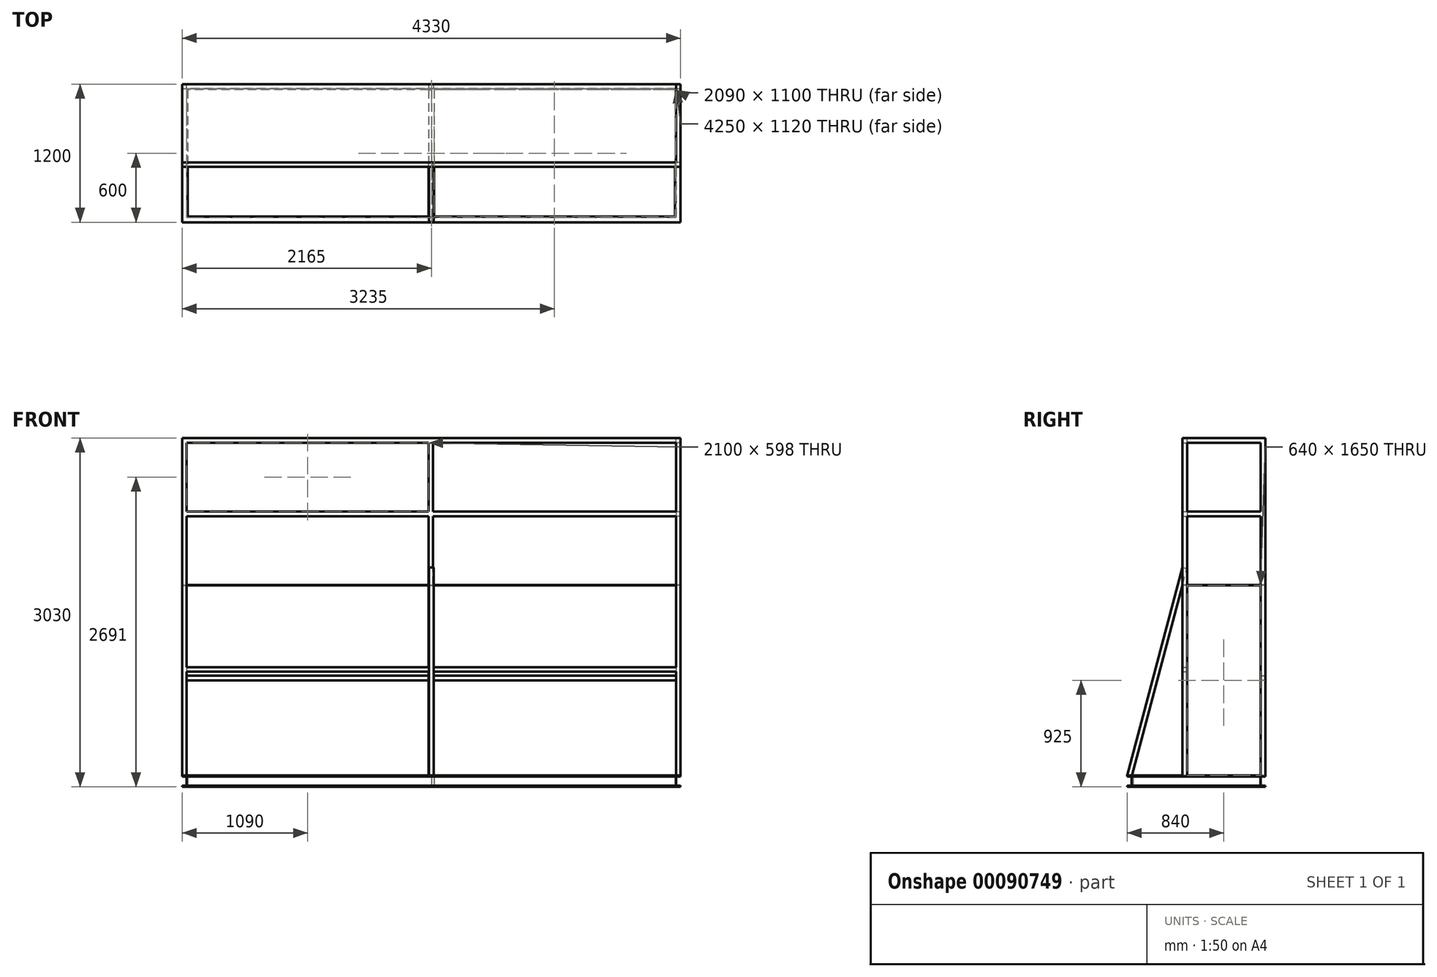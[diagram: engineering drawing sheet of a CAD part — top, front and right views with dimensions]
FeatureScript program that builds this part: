
annotation { "Feature Type Name" : "Feature", "Feature Type Description" : "" }
export const myFeature = defineFeature(function(context is Context, id is Id, definition is map)
    precondition{}
    {
        {
            var Q0;
            Q0=qCreatedBy(makeId("Top.planeOp"),FACE);
            var sketch = newSketch(context, id + "F0", { "sketchPlane" : qUnion([Q0])});
            skLineSegment(sketch, "E0.rect.bottom", {"start": v(2165, 600) * mm, "end": v(-2165, 600) * mm});
            skLineSegment(sketch, "E0.rect.top", {"start": v(2165, -600) * mm, "end": v(-2165, -600) * mm});
            skLineSegment(sketch, "E0.rect.left", {"start": v(2165, 600) * mm, "end": v(2165, -600) * mm});
            skLineSegment(sketch, "E0.rect.right", {"start": v(-2165, 600) * mm, "end": v(-2165, -600) * mm});
            skPoint(sketch, "E0.rect.middle", {"position": v(0, 0) * mm});
            skLineSegment(sketch, "E1.rect.bottom", {"start": v(2115, 550) * mm, "end": v(25, 550) * mm});
            skLineSegment(sketch, "E1.rect.top", {"start": v(2115, -550) * mm, "end": v(25, -550) * mm});
            skLineSegment(sketch, "E1.rect.left", {"start": v(2115, 550) * mm, "end": v(2115, -550) * mm});
            skLineSegment(sketch, "E1.rect.right", {"start": v(-2115, 550) * mm, "end": v(-2115, -550) * mm});
            skLineSegment(sketch, "E2.rect.left", {"start": v(25, 550) * mm, "end": v(25, -550) * mm});
            skLineSegment(sketch, "E2.rect.right", {"start": v(-25, 550) * mm, "end": v(-25, -550) * mm});
            skLineSegment(sketch, "E3.trimOffspring", {"start": v(-25, 550) * mm, "end": v(-2115, 550) * mm});
            skLineSegment(sketch, "E4.trimOffspring", {"start": v(-25, -550) * mm, "end": v(-2115, -550) * mm});
            skSolve(sketch);
        }
        {
            var Q0;
            Q0=makeQuery(id+"F0.imprint","IMPRINT",FACE,{"disambiguationData":[TD([[makeQuery(id+"F0.imprint","IMPRINT",EDGE,{"derivedFrom":sQuery(id+"F0.wireOp",EDGE,"E0.rect.bottom")}),1.0]])]});
            extrude(context, id + "F1", {"entities" : qUnion([Q0]), "depth" : 100 * mm});
        }
        {
            var Q0;
            Q0=makeQuery(id+"F1.opExtrude","SWEPT_FACE",FACE,{"disambiguationData":[OSD([sQuery(id+"F0.wireOp",EDGE,"E0.rect.right")])]});
            var sketch = newSketch(context, id + "F2", { "sketchPlane" : qUnion([Q0])});
            skLineSegment(sketch, "E5.bottom", {"start": v(-600, 90) * mm, "end": v(-560, 90) * mm});
            skLineSegment(sketch, "E5.top", {"start": v(-600, 10) * mm, "end": v(-560, 10) * mm});
            skLineSegment(sketch, "E5.left", {"start": v(-600, 90) * mm, "end": v(-600, 10) * mm});
            skLineSegment(sketch, "E5.right", {"start": v(-560, 90) * mm, "end": v(-560, 10) * mm});
            skLineSegment(sketch, "E6.bottom", {"start": v(600, 90) * mm, "end": v(560, 90) * mm});
            skLineSegment(sketch, "E6.top", {"start": v(600, 10) * mm, "end": v(560, 10) * mm});
            skLineSegment(sketch, "E6.left", {"start": v(600, 90) * mm, "end": v(600, 10) * mm});
            skLineSegment(sketch, "E6.right", {"start": v(560, 90) * mm, "end": v(560, 10) * mm});
            skSolve(sketch);
        }
        {
            var Q0;
            Q0=makeQuery(id+"F2.imprint","IMPRINT",FACE,{"disambiguationData":[TD([[makeQuery(id+"F2.imprint","IMPRINT",EDGE,{"derivedFrom":sQuery(id+"F2.wireOp",EDGE,"E5.bottom")}),-1.0]])]});
            var Q1;
            Q1=makeQuery(id+"F2.imprint","IMPRINT",FACE,{"disambiguationData":[TD([[makeQuery(id+"F2.imprint","IMPRINT",EDGE,{"derivedFrom":sQuery(id+"F2.wireOp",EDGE,"E6.bottom")}),1.0]])]});
            extrude(context, id + "F3", {"entities" : qUnion([Q0, Q1]), "operationType" : NewBodyOperationType.REMOVE, "endBound" : BoundingType.THROUGH_ALL, "oppositeDirection" : true, "depth" : 25 * mm});
        }
        {
            var Q0;
            Q0=makeQuery(id+"F3.boolean.opBoolean","COPY",FACE,{"derivedFrom":makeQuery(id+"F3.opExtrude","SWEPT_FACE",FACE,{"disambiguationData":[OSD([sQuery(id+"F2.wireOp",EDGE,"E6.right")])]})});
            var sketch = newSketch(context, id + "F4", { "sketchPlane" : qUnion([Q0])});
            skLineSegment(sketch, "E7.bottom", {"start": v(2165, 90) * mm, "end": v(2125, 90) * mm});
            skLineSegment(sketch, "E7.top", {"start": v(2165, 10) * mm, "end": v(2125, 10) * mm});
            skLineSegment(sketch, "E7.left", {"start": v(2165, 90) * mm, "end": v(2165, 10) * mm});
            skLineSegment(sketch, "E7.right", {"start": v(2125, 90) * mm, "end": v(2125, 10) * mm});
            skLineSegment(sketch, "E8.bottom", {"start": v(-2165, 90) * mm, "end": v(-2125, 90) * mm});
            skLineSegment(sketch, "E8.top", {"start": v(-2165, 10) * mm, "end": v(-2125, 10) * mm});
            skLineSegment(sketch, "E8.left", {"start": v(-2165, 90) * mm, "end": v(-2165, 10) * mm});
            skLineSegment(sketch, "E8.right", {"start": v(-2125, 90) * mm, "end": v(-2125, 10) * mm});
            skSolve(sketch);
        }
        {
            var Q0;
            Q0=makeQuery(id+"F4.imprint","IMPRINT",FACE,{"disambiguationData":[TD([[makeQuery(id+"F4.imprint","IMPRINT",EDGE,{"derivedFrom":sQuery(id+"F4.wireOp",EDGE,"E7.bottom")}),1.0]])]});
            var Q1;
            Q1=makeQuery(id+"F4.imprint","IMPRINT",FACE,{"disambiguationData":[TD([[makeQuery(id+"F4.imprint","IMPRINT",EDGE,{"derivedFrom":sQuery(id+"F4.wireOp",EDGE,"E8.bottom")}),1.0]])]});
            extrude(context, id + "F5", {"entities" : qUnion([Q0, Q1]), "operationType" : NewBodyOperationType.REMOVE, "endBound" : BoundingType.THROUGH_ALL, "oppositeDirection" : true, "depth" : 25 * mm});
        }
        {
            var Q0;
            Q0=qCreatedBy(makeId("Top.planeOp"),FACE);
            cPlane(context, id + "F6", {"entities" : qUnion([Q0]), "cplaneType" : CPlaneType.OFFSET, "offset" : 1750 * mm, "width" : 150 * mm, "height" : 150 * mm});
        }
        {
            var Q0;
            Q0=qCreatedBy(makeId("Front.planeOp"),FACE);
            var sketch = newSketch(context, id + "F7", { "sketchPlane" : qUnion([Q0])});
            skLineSegment(sketch, "E9.bottom", {"start": v(0, 10) * mm, "end": v(-90, 10) * mm});
            skLineSegment(sketch, "E9.top", {"start": v(0, 90) * mm, "end": v(-90, 90) * mm});
            skLineSegment(sketch, "E9.left", {"start": v(0, 10) * mm, "end": v(0, 90) * mm});
            skLineSegment(sketch, "E9.right", {"start": v(-90, 10) * mm, "end": v(-90, 90) * mm});
            skSolve(sketch);
        }
        {
            var Q0;
            Q0=qSketchRegion(id+"F7",true);
            var Q1;
            Q1=makeQuery(id+"F1.opExtrude","SWEPT_FACE",FACE,{"disambiguationData":[OSD([sQuery(id+"F0.wireOp",EDGE,"E3.trimOffspring")])]});
            var Q2;
            Q2=makeQuery(id+"F1.opExtrude","SWEPT_FACE",FACE,{"disambiguationData":[OSD([sQuery(id+"F0.wireOp",EDGE,"E4.trimOffspring")])]});
            extrude(context, id + "F8", {"entities" : qUnion([Q0]), "operationType" : NewBodyOperationType.REMOVE, "endBound" : BoundingType.UP_TO_SURFACE, "oppositeDirection" : true, "endBoundEntityFace" : qUnion([Q1]), "depth" : 25 * mm, "hasSecondDirection" : true, "secondDirectionBound" : SecondDirectionBoundingType.UP_TO_SURFACE, "secondDirectionOppositeDirection" : false, "secondDirectionBoundEntityFace" : qUnion([Q2]), "secondDirectionDepth" : 25 * mm});
        }
        {
            var Q0;
            Q0=makeQuery(id+"F1.opExtrude","CAP_FACE",FACE,{"disambiguationData":[OSD([sQuery(id+"F0.wireOp",EDGE,"E0.rect.bottom"),sQuery(id+"F0.wireOp",EDGE,"E0.rect.top"),sQuery(id+"F0.wireOp",EDGE,"E0.rect.left"),sQuery(id+"F0.wireOp",EDGE,"E0.rect.right"),sQuery(id+"F0.wireOp",EDGE,"E1.rect.bottom"),sQuery(id+"F0.wireOp",EDGE,"E1.rect.top"),sQuery(id+"F0.wireOp",EDGE,"E1.rect.left"),sQuery(id+"F0.wireOp",EDGE,"E1.rect.right"),sQuery(id+"F0.wireOp",EDGE,"E2.rect.left"),sQuery(id+"F0.wireOp",EDGE,"E2.rect.right"),sQuery(id+"F0.wireOp",EDGE,"E3.trimOffspring"),sQuery(id+"F0.wireOp",EDGE,"E4.trimOffspring")])],"isStart":false});
            var sketch = newSketch(context, id + "F9", { "sketchPlane" : qUnion([Q0])});
            skLineSegment(sketch, "E10.bottom", {"start": v(-2165, 600) * mm, "end": v(-2125, 600) * mm});
            skLineSegment(sketch, "E10.top", {"start": v(-2165, 560) * mm, "end": v(-2125, 560) * mm});
            skLineSegment(sketch, "E10.left", {"start": v(-2165, 600) * mm, "end": v(-2165, 560) * mm});
            skLineSegment(sketch, "E10.right", {"start": v(-2125, 600) * mm, "end": v(-2125, 560) * mm});
            skLineSegment(sketch, "E11.bottom", {"start": v(2165, 600) * mm, "end": v(2125, 600) * mm});
            skLineSegment(sketch, "E11.top", {"start": v(2165, 560) * mm, "end": v(2125, 560) * mm});
            skLineSegment(sketch, "E11.left", {"start": v(2165, 600) * mm, "end": v(2165, 560) * mm});
            skLineSegment(sketch, "E11.right", {"start": v(2125, 600) * mm, "end": v(2125, 560) * mm});
            skLineSegment(sketch, "E12.bottom", {"start": v(-20, 600) * mm, "end": v(20, 600) * mm});
            skLineSegment(sketch, "E12.top", {"start": v(-20, 560) * mm, "end": v(20, 560) * mm});
            skLineSegment(sketch, "E12.left", {"start": v(-20, 600) * mm, "end": v(-20, 560) * mm});
            skLineSegment(sketch, "E12.right", {"start": v(20, 600) * mm, "end": v(20, 560) * mm});
            skLineSegment(sketch, "E13.bottom", {"start": v(-2165, -80) * mm, "end": v(-2125, -80) * mm});
            skLineSegment(sketch, "E13.top", {"start": v(-2165, -120) * mm, "end": v(-2125, -120) * mm});
            skLineSegment(sketch, "E13.left", {"start": v(-2165, -80) * mm, "end": v(-2165, -120) * mm});
            skLineSegment(sketch, "E13.right", {"start": v(-2125, -80) * mm, "end": v(-2125, -120) * mm});
            skLineSegment(sketch, "E14.bottom", {"start": v(-25, -80) * mm, "end": v(15, -80) * mm});
            skLineSegment(sketch, "E14.top", {"start": v(-25, -120) * mm, "end": v(15, -120) * mm});
            skLineSegment(sketch, "E14.left", {"start": v(-25, -80) * mm, "end": v(-25, -120) * mm});
            skLineSegment(sketch, "E14.right", {"start": v(15, -80) * mm, "end": v(15, -120) * mm});
            skLineSegment(sketch, "E15.bottom", {"start": v(2165, -80) * mm, "end": v(2125, -80) * mm});
            skLineSegment(sketch, "E15.top", {"start": v(2165, -120) * mm, "end": v(2125, -120) * mm});
            skLineSegment(sketch, "E15.left", {"start": v(2165, -80) * mm, "end": v(2165, -120) * mm});
            skLineSegment(sketch, "E15.right", {"start": v(2125, -80) * mm, "end": v(2125, -120) * mm});
            skSolve(sketch);
        }
        {
            var Q0;
            Q0=makeQuery(id+"F9.imprint","IMPRINT",FACE,{"disambiguationData":[TD([[makeQuery(id+"F9.imprint","IMPRINT",EDGE,{"derivedFrom":sQuery(id+"F9.wireOp",EDGE,"E13.bottom")}),-1.0]])]});
            var Q1;
            Q1=makeQuery(id+"F9.imprint","IMPRINT",FACE,{"disambiguationData":[TD([[makeQuery(id+"F9.imprint","IMPRINT",EDGE,{"derivedFrom":sQuery(id+"F9.wireOp",EDGE,"E14.bottom")}),-1.0]])]});
            var Q2;
            Q2=makeQuery(id+"F9.imprint","IMPRINT",FACE,{"disambiguationData":[TD([[makeQuery(id+"F9.imprint","IMPRINT",EDGE,{"derivedFrom":sQuery(id+"F9.wireOp",EDGE,"E11.bottom")}),1.0]])]});
            var Q3;
            Q3=makeQuery(id+"F9.imprint","IMPRINT",FACE,{"disambiguationData":[TD([[makeQuery(id+"F9.imprint","IMPRINT",EDGE,{"derivedFrom":sQuery(id+"F9.wireOp",EDGE,"E15.bottom")}),1.0]])]});
            extrude(context, id + "F10", {"entities" : qUnion([Q0, Q1, Q2, Q3]), "operationType" : NewBodyOperationType.ADD, "depth" : 2930 * mm});
        }
        {
            var Q0;
            Q0=qCreatedBy(id+"F6.planeOp",FACE);
            var sketch = newSketch(context, id + "F11", { "sketchPlane" : qUnion([Q0])});
            skLineSegment(sketch, "E16.bottom", {"start": v(-2165, 600) * mm, "end": v(2165, 600) * mm});
            skLineSegment(sketch, "E16.top", {"start": v(-2165, -120) * mm, "end": v(2165, -120) * mm});
            skLineSegment(sketch, "E16.left", {"start": v(-2165, 600) * mm, "end": v(-2165, -120) * mm});
            skLineSegment(sketch, "E16.right", {"start": v(2165, 600) * mm, "end": v(2165, -120) * mm});
            skSolve(sketch);
        }
        {
            var Q0;
            Q0=qSketchRegion(id+"F11",true);
            extrude(context, id + "F12", {"entities" : qUnion([Q0]), "operationType" : NewBodyOperationType.ADD, "depth" : 4 * mm});
        }
        {
            var Q0;
            Q0=qSketchRegion(id+"F9",true);
            extrude(context, id + "F13", {"entities" : qUnion([Q0]), "operationType" : NewBodyOperationType.ADD, "depth" : 1650 * mm});
        }
        {
            var Q0;
            {var subQ1=sQuery(id+"F0.wireOp",EDGE,"E0.rect.left");Q0=makeQuery(id+"F12.boolean.opBoolean","MERGE",FACE,{"derivedFrom":[makeQuery(id+"F10.boolean.opBoolean","MERGE",FACE,{"derivedFrom":[makeQuery(id+"F5.boolean.opBoolean","SPLIT",FACE,{"disambiguationData":[TD([makeQuery(id+"F3.boolean.opBoolean","COPY",FACE,{"derivedFrom":makeQuery(id+"F3.opExtrude","SWEPT_FACE",FACE,{"disambiguationData":[OSD([sQuery(id+"F2.wireOp",EDGE,"E5.bottom")])]})})])],"derivedFrom":makeQuery(id+"F1.opExtrude","SWEPT_FACE",FACE,{"disambiguationData":[OSD([subQ1])]})}),makeQuery(id+"F10.opExtrude","SWEPT_FACE",FACE,{"disambiguationData":[OSD([sQuery(id+"F9.wireOp",EDGE,"E11.left")])]}),makeQuery(id+"F10.opExtrude","SWEPT_FACE",FACE,{"disambiguationData":[OSD([sQuery(id+"F9.wireOp",EDGE,"E15.left")])]})]}),makeQuery(id+"F12.opExtrude","SWEPT_FACE",FACE,{"disambiguationData":[OSD([sQuery(id+"F11.wireOp",EDGE,"E16.right")])]})]});}
            var sketch = newSketch(context, id + "F14", { "sketchPlane" : qUnion([Q0])});
            skLineSegment(sketch, "E17.bottom", {"start": v(-120, 3030) * mm, "end": v(-80, 3030) * mm});
            skLineSegment(sketch, "E17.top", {"start": v(-120, 2990) * mm, "end": v(-80, 2990) * mm});
            skLineSegment(sketch, "E17.left", {"start": v(-80, 3030) * mm, "end": v(-80, 2990) * mm});
            skLineSegment(sketch, "E17.right", {"start": v(-120, 3030) * mm, "end": v(-120, 2990) * mm});
            skLineSegment(sketch, "E18.left", {"start": v(600, 965) * mm, "end": v(600, 925) * mm});
            skLineSegment(sketch, "E18.right", {"start": v(-80, 1040) * mm, "end": v(-80, 1000) * mm});
            skLineSegment(sketch, "E19.bottom", {"start": v(-120, 1040) * mm, "end": v(-80, 1040) * mm});
            skLineSegment(sketch, "E19.top", {"start": v(-120, 1000) * mm, "end": v(-80, 1000) * mm});
            skLineSegment(sketch, "E19.right", {"start": v(-120, 1040) * mm, "end": v(-120, 1000) * mm});
            skLineSegment(sketch, "E20.bottom", {"start": v(-120, 2392) * mm, "end": v(-80, 2392) * mm});
            skLineSegment(sketch, "E20.top", {"start": v(-120, 2352) * mm, "end": v(-80, 2352) * mm});
            skLineSegment(sketch, "E20.left", {"start": v(-80, 2392) * mm, "end": v(-80, 2352) * mm});
            skLineSegment(sketch, "E20.right", {"start": v(-120, 2392) * mm, "end": v(-120, 2352) * mm});
            skLineSegment(sketch, "E21", {"start": v(560, 965) * mm, "end": v(600, 965) * mm});
            skLineSegment(sketch, "E22", {"start": v(560, 965) * mm, "end": v(560, 925) * mm});
            skLineSegment(sketch, "E23", {"start": v(600, 925) * mm, "end": v(560, 925) * mm});
            skSolve(sketch);
        }
        {
            var Q0;
            Q0=qSketchRegion(id+"F14",true);
            extrude(context, id + "F15", {"entities" : qUnion([Q0]), "operationType" : NewBodyOperationType.ADD, "oppositeDirection" : true, "depth" : 4300 * mm});
        }
        {
            var Q0;
            Q0=makeQuery(id+"F15.boolean.opBoolean","MERGE",FACE,{"derivedFrom":[makeQuery(id+"F12.boolean.opBoolean","MERGE",FACE,{"derivedFrom":[makeQuery(id+"F10.opExtrude","SWEPT_FACE",FACE,{"disambiguationData":[OSD([sQuery(id+"F9.wireOp",EDGE,"E13.top")])]}),makeQuery(id+"F10.opExtrude","SWEPT_FACE",FACE,{"disambiguationData":[OSD([sQuery(id+"F9.wireOp",EDGE,"E14.top")])]}),makeQuery(id+"F10.opExtrude","SWEPT_FACE",FACE,{"disambiguationData":[OSD([sQuery(id+"F9.wireOp",EDGE,"E15.top")])]}),makeQuery(id+"F12.opExtrude","SWEPT_FACE",FACE,{"disambiguationData":[OSD([sQuery(id+"F11.wireOp",EDGE,"E16.top")])]})]}),makeQuery(id+"F15.opExtrude","SWEPT_FACE",FACE,{"disambiguationData":[OSD([sQuery(id+"F14.wireOp",EDGE,"E17.right")])]}),makeQuery(id+"F15.opExtrude","SWEPT_FACE",FACE,{"disambiguationData":[OSD([sQuery(id+"F14.wireOp",EDGE,"E19.right")])]}),makeQuery(id+"F15.opExtrude","SWEPT_FACE",FACE,{"disambiguationData":[OSD([sQuery(id+"F14.wireOp",EDGE,"E20.right")])]})]});
            var sketch = newSketch(context, id + "F16", { "sketchPlane" : qUnion([Q0])});
            skLineSegment(sketch, "E24.left", {"start": v(2125, 3030) * mm, "end": v(2125, 2990) * mm});
            skLineSegment(sketch, "E24.right", {"start": v(2165, 3030) * mm, "end": v(2165, 2990) * mm});
            skLineSegment(sketch, "E25", {"start": v(2125, 3030) * mm, "end": v(2165, 3030) * mm});
            skLineSegment(sketch, "E26", {"start": v(2165, 2990) * mm, "end": v(2125, 2990) * mm});
            skLineSegment(sketch, "E27", {"start": v(2125, 2392) * mm, "end": v(2165, 2392) * mm});
            skLineSegment(sketch, "E28", {"start": v(2165, 2392) * mm, "end": v(2165, 2352) * mm});
            skLineSegment(sketch, "E29", {"start": v(2165, 2352) * mm, "end": v(2125, 2352) * mm});
            skLineSegment(sketch, "E30", {"start": v(2125, 2352) * mm, "end": v(2125, 2392) * mm});
            skSolve(sketch);
        }
        {
            var Q0;
            Q0=makeQuery(id+"F16.imprint","IMPRINT",FACE,{"disambiguationData":[TD([[makeQuery(id+"F16.imprint","IMPRINT",EDGE,{"derivedFrom":sQuery(id+"F16.wireOp",EDGE,"E27")}),-1.0]])]});
            var Q1;
            Q1=makeQuery(id+"F16.imprint","IMPRINT",FACE,{"disambiguationData":[TD([[makeQuery(id+"F16.imprint","IMPRINT",EDGE,{"derivedFrom":sQuery(id+"F16.wireOp",EDGE,"E24.left")}),1.0]])]});
            extrude(context, id + "F17", {"entities" : qUnion([Q0, Q1]), "operationType" : NewBodyOperationType.ADD, "oppositeDirection" : true, "depth" : 720 * mm});
        }
        {
            var Q0;
            Q0=qCreatedBy(makeId("Right.planeOp"),FACE);
            var sketch = newSketch(context, id + "F18", { "sketchPlane" : qUnion([Q0])});
            skLineSegment(sketch, "E31", {"start": v(-120.36, 1905.24) * mm, "end": v(-599.6, 98.65) * mm});
            skLineSegment(sketch, "E32.0", {"start": v(-81.7, 1894.99) * mm, "end": v(-558.34, 98.2) * mm});
            skLineSegment(sketch, "E33", {"start": v(-558.34, 98.2) * mm, "end": v(-599.6, 98.65) * mm});
            skLineSegment(sketch, "E34", {"start": v(-120.36, 1905.24) * mm, "end": v(-81.7, 1894.99) * mm});
            skSolve(sketch);
        }
        {
            var Q0;
            Q0=makeQuery(id+"F18.imprint","IMPRINT",FACE,{"disambiguationData":[TD([[makeQuery(id+"F18.imprint","IMPRINT",EDGE,{"derivedFrom":sQuery(id+"F18.wireOp",EDGE,"E31")}),1.0]])]});
            extrude(context, id + "F19", {"entities" : qUnion([Q0]), "operationType" : NewBodyOperationType.ADD, "endBound" : BoundingType.SYMMETRIC, "depth" : 40 * mm});
        }
    });
